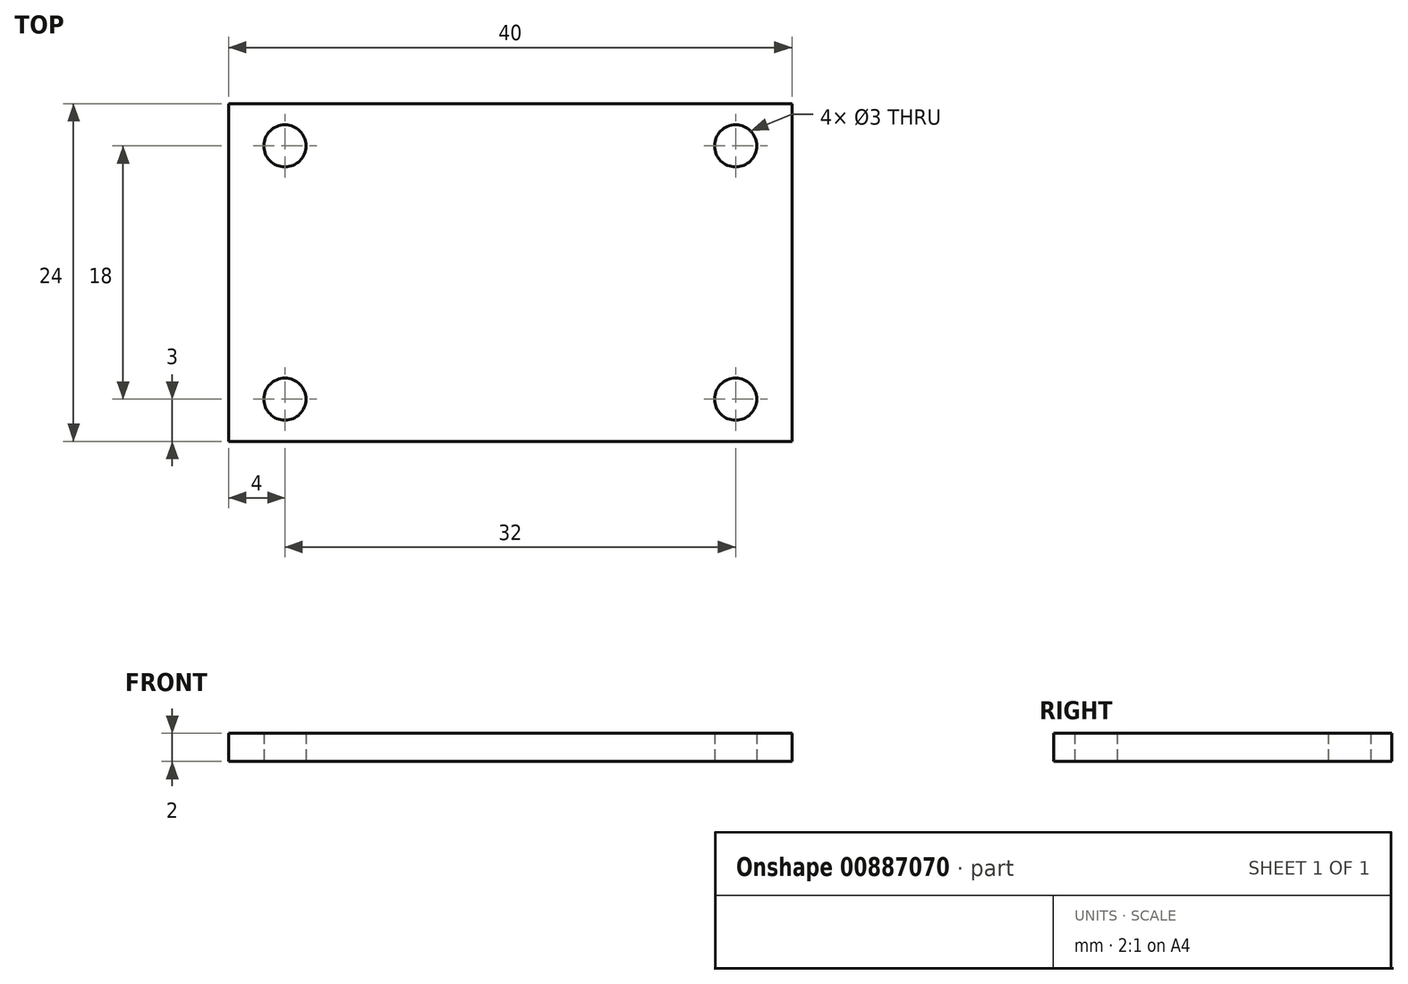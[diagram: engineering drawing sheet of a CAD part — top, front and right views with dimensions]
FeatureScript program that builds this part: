
annotation { "Feature Type Name" : "Feature", "Feature Type Description" : "" }
export const myFeature = defineFeature(function(context is Context, id is Id, definition is map)
    precondition{}
    {
        {
            var Q0;
            Q0=qCreatedBy(makeId("Top.planeOp"),FACE);
            var sketch = newSketch(context, id + "F0", { "sketchPlane" : qUnion([Q0])});
            skLineSegment(sketch, "E0.bottom", {"start": v(20, -12) * mm, "end": v(-20, -12) * mm});
            skLineSegment(sketch, "E0.top", {"start": v(20, 12) * mm, "end": v(-20, 12) * mm});
            skLineSegment(sketch, "E0.left", {"start": v(20, -12) * mm, "end": v(20, 12) * mm});
            skLineSegment(sketch, "E0.right", {"start": v(-20, -12) * mm, "end": v(-20, 12) * mm});
            skPoint(sketch, "E0.middle", {"position": v(0, 0) * mm});
            skSolve(sketch);
        }
        {
            var Q0;
            Q0=makeQuery(id+"F0.imprint","IMPRINT",FACE,{"disambiguationData":[TD([[makeQuery(id+"F0.imprint","IMPRINT",EDGE,{"derivedFrom":sQuery(id+"F0.wireOp",EDGE,"E0.bottom")}),-1.0]])]});
            extrude(context, id + "F1", {"entities" : qUnion([Q0]), "depth" : 2 * mm, "offsetDistance" : 25 * mm});
        }
        {
            var Q0;
            Q0=qCreatedBy(makeId("Top.planeOp"),FACE);
            var sketch = newSketch(context, id + "F2", { "sketchPlane" : qUnion([Q0])});
            skLineSegment(sketch, "E1.bottom", {"start": v(16, 9) * mm, "end": v(-16, 9) * mm, "construction": true});
            skLineSegment(sketch, "E1.top", {"start": v(16, -9) * mm, "end": v(-16, -9) * mm, "construction": true});
            skLineSegment(sketch, "E1.left", {"start": v(16, 9) * mm, "end": v(16, -9) * mm, "construction": true});
            skLineSegment(sketch, "E1.right", {"start": v(-16, 9) * mm, "end": v(-16, -9) * mm, "construction": true});
            skPoint(sketch, "E1.middle", {"position": v(0, 0) * mm});
            skCircle(sketch, "E2", {"center": v(-16, -9) * mm, "radius": 1.5 * mm});
            skCircle(sketch, "E3", {"center": v(16, -9) * mm, "radius": 1.5 * mm});
            skCircle(sketch, "E4", {"center": v(16, 9) * mm, "radius": 1.5 * mm});
            skCircle(sketch, "E5", {"center": v(-16, 9) * mm, "radius": 1.5 * mm});
            skSolve(sketch);
        }
        {
            var Q0;
            Q0=qSketchRegion(id+"F2",true);
            extrude(context, id + "F3", {"entities" : qUnion([Q0]), "operationType" : NewBodyOperationType.REMOVE, "depth" : 25 * mm, "offsetDistance" : 25 * mm});
        }
    });
